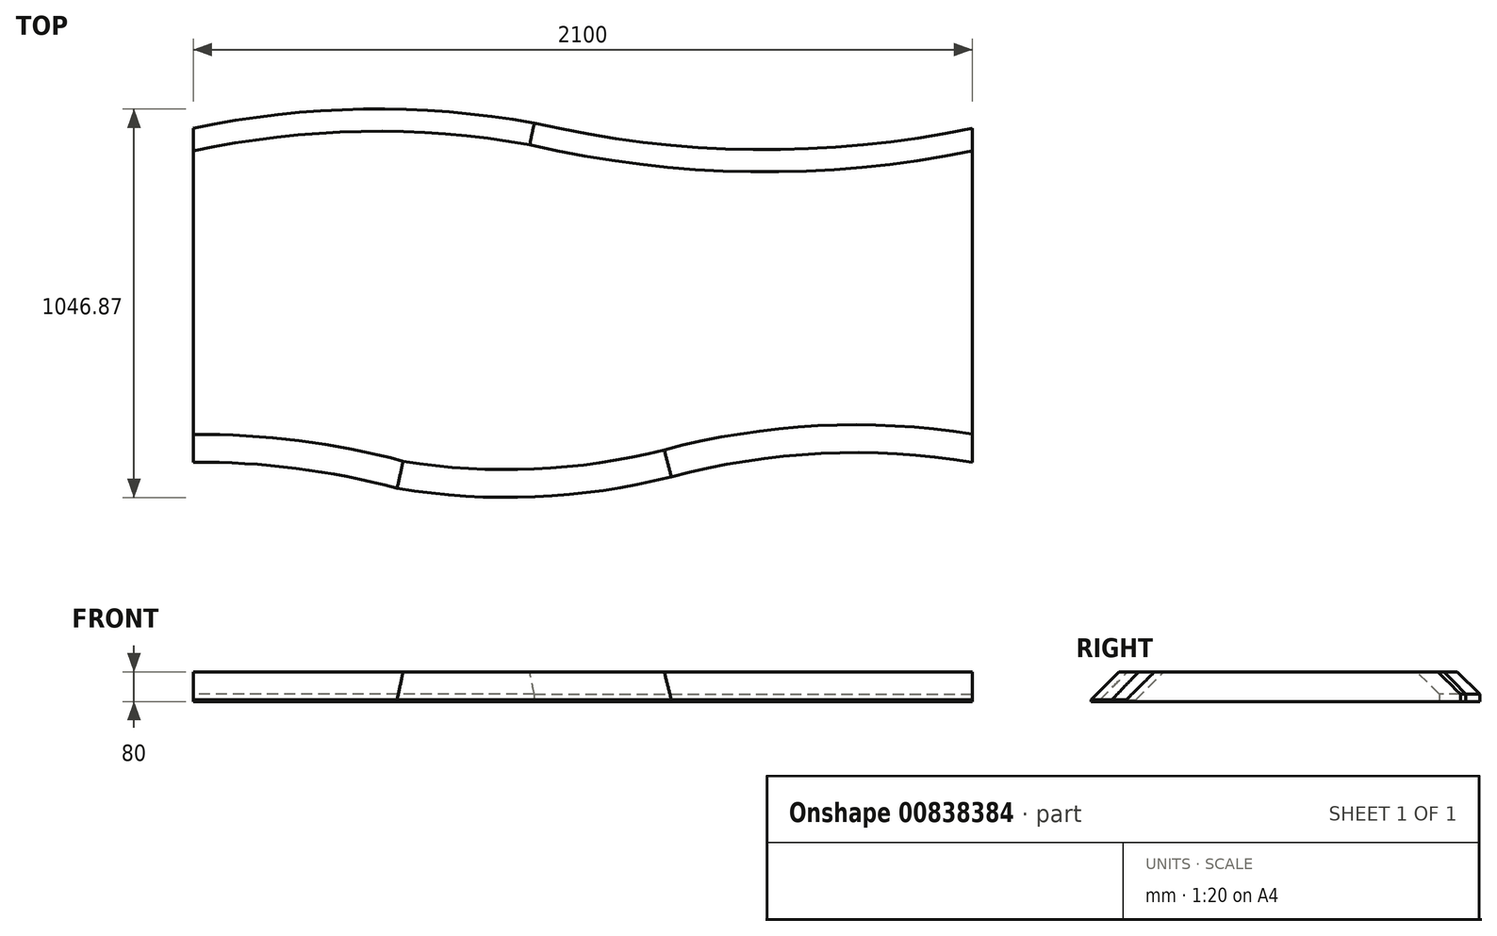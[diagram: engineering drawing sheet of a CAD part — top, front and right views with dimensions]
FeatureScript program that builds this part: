
annotation { "Feature Type Name" : "Feature", "Feature Type Description" : "" }
export const myFeature = defineFeature(function(context is Context, id is Id, definition is map)
    precondition{}
    {
        {
            var Q0;
            Q0=qCreatedBy(makeId("Top.planeOp"),FACE);
            var sketch = newSketch(context, id + "F0", { "sketchPlane" : qUnion([Q0])});
            skLineSegment(sketch, "E0.left", {"start": v(0, 0) * mm, "end": v(0, 900) * mm});
            skLineSegment(sketch, "E0.right", {"start": v(2100, 0) * mm, "end": v(2100, 900) * mm});
            skArc(sketch, "E1", {"start": v(918.9, 914.2) * mm, "mid": v(458.76, 951.64) * mm, "end": v(0, 900) * mm});
            skArc(sketch, "E2", {"start": v(918.9, 914.2) * mm, "mid": v(1508.68, 842.77) * mm, "end": v(2100, 900) * mm});
            skArc(sketch, "E3", {"start": v(549.46, -70.59) * mm, "mid": v(277.12, -16.7) * mm, "end": v(0, 0) * mm});
            skArc(sketch, "E4", {"start": v(549.46, -70.59) * mm, "mid": v(920.44, -93.34) * mm, "end": v(1288.18, -39.33) * mm});
            skArc(sketch, "E5", {"start": v(2100, 0) * mm, "mid": v(1692, 23.48) * mm, "end": v(1288.18, -39.33) * mm});
            skSolve(sketch);
        }
        {
            var Q0;
            Q0 = qSketchRegion(id + "F0", true);
            extrude(context, id + "F1", {"entities" : qUnion([Q0]), "depth" : 80 * mm, "offsetDistance" : 25 * mm});
        }
        {
            var Q0;
            Q0=makeQuery(id+"F1.opExtrude","CAP_EDGE",EDGE,{"disambiguationData":[OSD([sQuery(id+"F0.wireOp",EDGE,"E3")])],"isStart":false});
            var Q1;
            Q1=makeQuery(id+"F1.opExtrude","CAP_EDGE",EDGE,{"disambiguationData":[OSD([sQuery(id+"F0.wireOp",EDGE,"E4")])],"isStart":false});
            var Q2;
            Q2=makeQuery(id+"F1.opExtrude","CAP_EDGE",EDGE,{"disambiguationData":[OSD([sQuery(id+"F0.wireOp",EDGE,"E5")])],"isStart":false});
            chamfer(context, id + "F2", {"entities" : qUnion([Q0, Q1, Q2]), "width" : 75 * mm, "tangentPropagation" : true});
        }
        {
            var Q0;
            Q0=makeQuery(id+"F1.opExtrude","CAP_EDGE",EDGE,{"disambiguationData":[OSD([sQuery(id+"F0.wireOp",EDGE,"E2")])],"isStart":false});
            var Q1;
            Q1=makeQuery(id+"F1.opExtrude","CAP_EDGE",EDGE,{"disambiguationData":[OSD([sQuery(id+"F0.wireOp",EDGE,"E1")])],"isStart":false});
            chamfer(context, id + "F3", {"entities" : qUnion([Q0, Q1]), "width" : 60 * mm, "tangentPropagation" : true});
        }
    });
